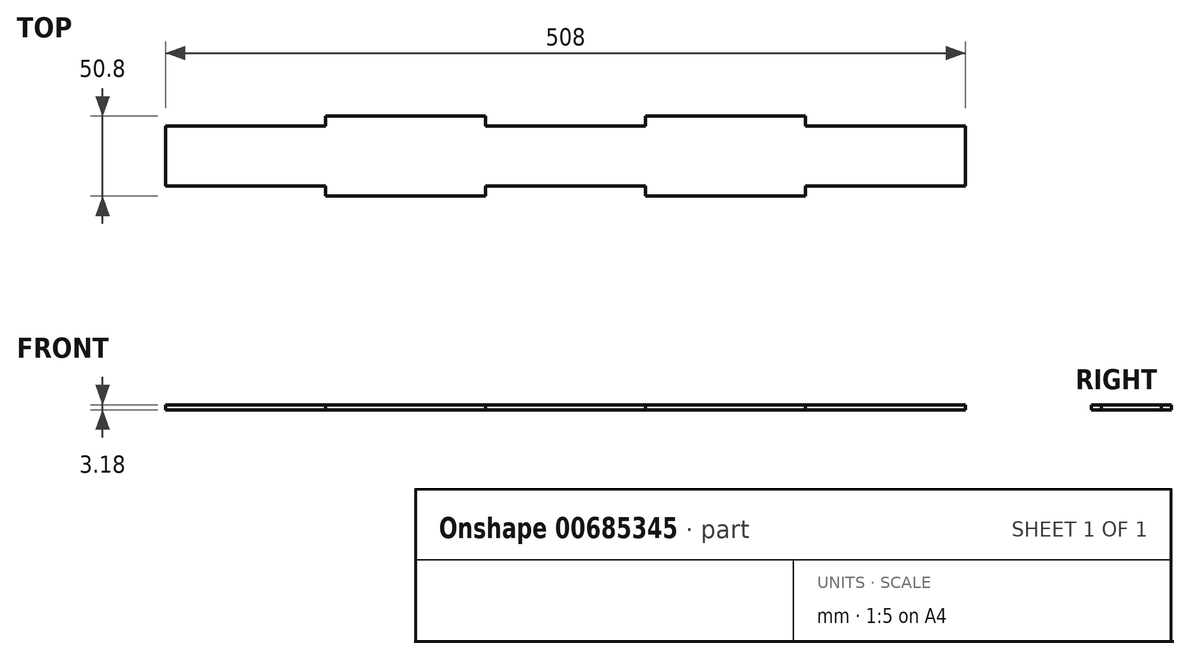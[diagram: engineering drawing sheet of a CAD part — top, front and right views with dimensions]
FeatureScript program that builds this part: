
annotation { "Feature Type Name" : "Feature", "Feature Type Description" : "" }
export const myFeature = defineFeature(function(context is Context, id is Id, definition is map)
    precondition{}
    {
        {
            var Q0;
            Q0=qCreatedBy(makeId("Top.planeOp"),FACE);
            var sketch = newSketch(context, id + "F0", { "sketchPlane" : qUnion([Q0])});
            skLineSegment(sketch, "E0.bottom", {"start": v(0, 0) * mm, "end": v(508, 0) * mm});
            skLineSegment(sketch, "E0.top", {"start": v(0, 50.8) * mm, "end": v(508, 50.8) * mm});
            skLineSegment(sketch, "E0.left", {"start": v(0, 0) * mm, "end": v(0, 50.8) * mm});
            skLineSegment(sketch, "E0.right", {"start": v(508, 0) * mm, "end": v(508, 50.8) * mm});
            skSolve(sketch);
        }
        {
            var Q0;
            Q0=makeQuery(id+"F0.imprint","IMPRINT",FACE,{"disambiguationData":[TD([[makeQuery(id+"F0.imprint","IMPRINT",EDGE,{"derivedFrom":sQuery(id+"F0.wireOp",EDGE,"E0.bottom")}),1.0]])]});
            extrude(context, id + "F1", {"entities" : qUnion([Q0]), "depth" : 3.17 * mm, "offsetDistance" : 25.4 * mm});
        }
        {
            var Q0;
            Q0=makeQuery(id+"F1.opExtrude","CAP_FACE",FACE,{"disambiguationData":[OSD([sQuery(id+"F0.wireOp",EDGE,"E0.bottom"),sQuery(id+"F0.wireOp",EDGE,"E0.top"),sQuery(id+"F0.wireOp",EDGE,"E0.left"),sQuery(id+"F0.wireOp",EDGE,"E0.right")])],"isStart":false});
            var sketch = newSketch(context, id + "F2", { "sketchPlane" : qUnion([Q0])});
            skLineSegment(sketch, "E1.bottom", {"start": v(0, 0) * mm, "end": v(101.6, 0) * mm});
            skLineSegment(sketch, "E1.top", {"start": v(0, 6.35) * mm, "end": v(101.6, 6.35) * mm});
            skLineSegment(sketch, "E1.left", {"start": v(0, 0) * mm, "end": v(0, 6.35) * mm});
            skLineSegment(sketch, "E1.right", {"start": v(101.6, 0) * mm, "end": v(101.6, 6.35) * mm});
            skLineSegment(sketch, "E2.bottom", {"start": v(203.2, 0) * mm, "end": v(304.8, 0) * mm});
            skLineSegment(sketch, "E2.top", {"start": v(203.2, 6.35) * mm, "end": v(304.8, 6.35) * mm});
            skLineSegment(sketch, "E2.left", {"start": v(203.2, 0) * mm, "end": v(203.2, 6.35) * mm});
            skLineSegment(sketch, "E2.right", {"start": v(304.8, 0) * mm, "end": v(304.8, 6.35) * mm});
            skLineSegment(sketch, "E3.bottom", {"start": v(406.4, 0) * mm, "end": v(508, 0) * mm});
            skLineSegment(sketch, "E3.top", {"start": v(406.4, 6.35) * mm, "end": v(508, 6.35) * mm});
            skLineSegment(sketch, "E3.left", {"start": v(406.4, 0) * mm, "end": v(406.4, 6.35) * mm});
            skLineSegment(sketch, "E3.right", {"start": v(508, 0) * mm, "end": v(508, 6.35) * mm});
            skSolve(sketch);
        }
        {
            var Q0;
            Q0=makeQuery(id+"F2.imprint","IMPRINT",FACE,{"disambiguationData":[TD([[makeQuery(id+"F2.imprint","IMPRINT",EDGE,{"derivedFrom":sQuery(id+"F2.wireOp",EDGE,"E2.bottom")}),1.0]])]});
            var Q1;
            Q1=makeQuery(id+"F2.imprint","IMPRINT",FACE,{"disambiguationData":[TD([[makeQuery(id+"F2.imprint","IMPRINT",EDGE,{"derivedFrom":sQuery(id+"F2.wireOp",EDGE,"E3.bottom")}),1.0]])]});
            var Q2;
            Q2=makeQuery(id+"F2.imprint","IMPRINT",FACE,{"disambiguationData":[TD([[makeQuery(id+"F2.imprint","IMPRINT",EDGE,{"derivedFrom":sQuery(id+"F2.wireOp",EDGE,"E1.bottom")}),1.0]])]});
            extrude(context, id + "F3", {"entities" : qUnion([Q0, Q1, Q2]), "operationType" : NewBodyOperationType.REMOVE, "oppositeDirection" : true, "depth" : 25.4 * mm, "offsetDistance" : 25.4 * mm});
        }
        {
            var Q0;
            Q0=makeQuery(id+"F1.opExtrude","CAP_FACE",FACE,{"disambiguationData":[OSD([sQuery(id+"F0.wireOp",EDGE,"E0.bottom"),sQuery(id+"F0.wireOp",EDGE,"E0.top"),sQuery(id+"F0.wireOp",EDGE,"E0.left"),sQuery(id+"F0.wireOp",EDGE,"E0.right")])],"isStart":false});
            var sketch = newSketch(context, id + "F4", { "sketchPlane" : qUnion([Q0])});
            skLineSegment(sketch, "E4.bottom", {"start": v(0, 50.8) * mm, "end": v(101.6, 50.8) * mm});
            skLineSegment(sketch, "E4.top", {"start": v(0, 44.45) * mm, "end": v(101.6, 44.45) * mm});
            skLineSegment(sketch, "E4.left", {"start": v(0, 50.8) * mm, "end": v(0, 44.45) * mm});
            skLineSegment(sketch, "E4.right", {"start": v(101.6, 50.8) * mm, "end": v(101.6, 44.45) * mm});
            skLineSegment(sketch, "E5.bottom", {"start": v(203.2, 50.8) * mm, "end": v(304.8, 50.8) * mm});
            skLineSegment(sketch, "E5.top", {"start": v(203.2, 44.45) * mm, "end": v(304.8, 44.45) * mm});
            skLineSegment(sketch, "E5.left", {"start": v(203.2, 50.8) * mm, "end": v(203.2, 44.45) * mm});
            skLineSegment(sketch, "E5.right", {"start": v(304.8, 50.8) * mm, "end": v(304.8, 44.45) * mm});
            skLineSegment(sketch, "E6.bottom", {"start": v(508, 50.8) * mm, "end": v(406.4, 50.8) * mm});
            skLineSegment(sketch, "E6.top", {"start": v(508, 44.45) * mm, "end": v(406.4, 44.45) * mm});
            skLineSegment(sketch, "E6.left", {"start": v(508, 50.8) * mm, "end": v(508, 44.45) * mm});
            skLineSegment(sketch, "E6.right", {"start": v(406.4, 50.8) * mm, "end": v(406.4, 44.45) * mm});
            skSolve(sketch);
        }
        {
            var Q0;
            Q0=makeQuery(id+"F4.imprint","IMPRINT",FACE,{"disambiguationData":[TD([[makeQuery(id+"F4.imprint","IMPRINT",EDGE,{"derivedFrom":sQuery(id+"F4.wireOp",EDGE,"E6.bottom")}),-1.0]])]});
            var Q1;
            Q1=makeQuery(id+"F4.imprint","IMPRINT",FACE,{"disambiguationData":[TD([[makeQuery(id+"F4.imprint","IMPRINT",EDGE,{"derivedFrom":sQuery(id+"F4.wireOp",EDGE,"E5.bottom")}),-1.0]])]});
            var Q2;
            Q2=makeQuery(id+"F4.imprint","IMPRINT",FACE,{"disambiguationData":[TD([[makeQuery(id+"F4.imprint","IMPRINT",EDGE,{"derivedFrom":sQuery(id+"F4.wireOp",EDGE,"E4.bottom")}),-1.0]])]});
            extrude(context, id + "F5", {"entities" : qUnion([Q0, Q1, Q2]), "operationType" : NewBodyOperationType.REMOVE, "oppositeDirection" : true, "depth" : 25.4 * mm, "offsetDistance" : 25.4 * mm});
        }
    });
